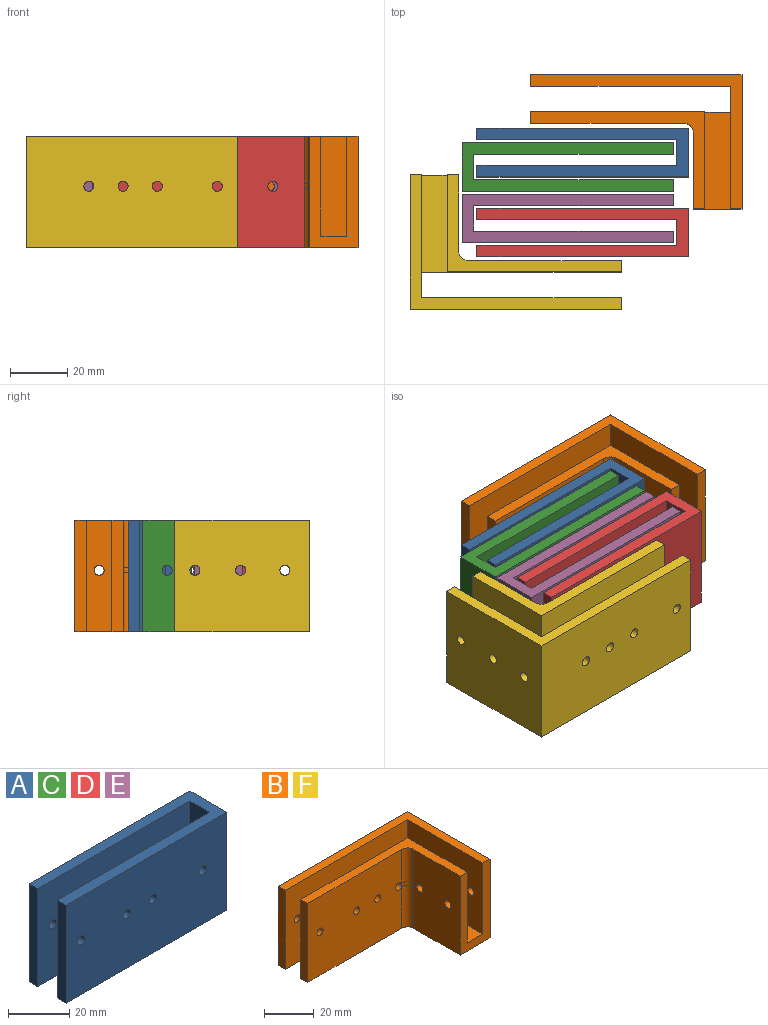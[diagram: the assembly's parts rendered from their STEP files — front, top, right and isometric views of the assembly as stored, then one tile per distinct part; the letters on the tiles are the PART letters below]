
ASSEMBLY  parts=6 mates=8
PART A: 19 faces, bbox 74x17x39 mm
  f0: plane 39x9mm, normal (-1,0,0), area 341.4mm2, adj f1,f7,f8,f9,f18
  f1: plane 70x39mm, normal (0,1,0), area 2691.5mm2, adj f0,f2,f8,f9,f14,f15,f16,f17
  f2: plane 39x4mm, normal (-1,0,0), area 156mm2, adj f1,f3,f8,f9
  f3: plane 74x39mm, normal (0,-1,0), area 2847.5mm2, adj f2,f4,f8,f9,f14,f15,f16,f17
  f4: plane 39x17mm, normal (1,0,0), area 653.4mm2, adj f3,f5,f8,f9,f18
  f5: plane 74x39mm, normal (0,1,0), area 2847.5mm2, adj f4,f6,f8,f9,f10,f11,f12,f13
  f6: plane 39x4mm, normal (-1,0,0), area 156mm2, adj f5,f7,f8,f9
  f7: plane 70x39mm, normal (0,-1,0), area 2691.5mm2, adj f0,f6,f8,f9,f10,f11,f12,f13
  f8: plane 74x17mm, normal (0,0,-1), area 628mm2, adj f0,f1,f2,f3,f4,f5,f6,f7
  f9: plane 74x17mm, normal (0,0,1), area 628mm2, adj f0,f1,f2,f3,f4,f5,f6,f7
  f10: cylinder r=1.75mm len=4mm, axis (0,-1,0), area 44mm2, adj f5,f7
  f11: cylinder r=1.75mm len=4mm, axis (0,-1,0), area 44mm2, adj f5,f7
  f12: cylinder r=1.75mm len=4mm, axis (0,-1,0), area 44mm2, adj f5,f7
  f13: cylinder r=1.75mm len=4mm, axis (0,-1,0), area 44mm2, adj f5,f7
  f14: cylinder r=1.75mm len=4mm, axis (0,-1,0), area 44mm2, adj f1,f3
  f15: cylinder r=1.75mm len=4mm, axis (0,-1,0), area 44mm2, adj f1,f3
  f16: cylinder r=1.75mm len=4mm, axis (0,-1,0), area 44mm2, adj f1,f3
  f17: cylinder r=1.75mm len=4mm, axis (0,-1,0), area 44mm2, adj f1,f3
  f18: cylinder r=1.75mm len=4mm, axis (-1,0,0), area 44mm2, adj f0,f4
PART B: 31 faces, bbox 74x47x39 mm
  f0: plane 34x9mm, normal (0,0,1), area 306mm2, adj f2,f3,f8,f12
  f1: plane 39x4mm, normal (-1,0,0), area 156mm2, adj f2,f10,f11,f13
  f2: plane 70x39mm, normal (0,1,0), area 2376.5mm2, adj f0,f1,f3,f11,f12,f13,f15,f16
  f3: plane 43x39mm, normal (-1,0,0), area 1512.1mm2, adj f0,f2,f4,f8,f11,f14,f25,f26
  f4: plane 70x39mm, normal (0,-1,0), area 2691.5mm2, adj f3,f5,f11,f14,f19,f20,f21,f22
  f5: plane 39x4mm, normal (-1,0,0), area 156mm2, adj f4,f6,f11,f14
  f6: plane 74x39mm, normal (0,1,0), area 2847.5mm2, adj f5,f7,f11,f14,f19,f20,f21,f22
  f7: plane 47x39mm, normal (1,0,0), area 1804.1mm2, adj f6,f8,f11,f14,f25,f26,f27
  f8: plane 39x17mm, normal (0,-1,0), area 348mm2, adj f0,f3,f7,f9,f11,f12,f13,f14
  f9: plane 39x26.51mm, normal (-1,0,0), area 1014.3mm2, adj f8,f11,f13,f23,f24,f28,f29,f30
  f10: plane 53.5x39mm, normal (0,-1,0), area 2048.3mm2, adj f1,f11,f13,f15,f16,f17,f18,f28
  f11: plane 74x47mm, normal (0,0,-1), area 1140.6mm2, adj f1,f2,f3,f4,f5,f6,f7,f8
  f12: plane 35x34mm, normal (1,0,0), area 1170.8mm2, adj f0,f2,f8,f13,f23,f24
  f13: plane 61x34mm, normal (0,0,1), area 366.6mm2, adj f1,f2,f8,f9,f10,f12,f30
  f14: plane 74x47mm, normal (0,0,1), area 468mm2, adj f3,f4,f5,f6,f7,f8
  f15: cylinder r=1.75mm len=4mm, axis (0,1,0), area 44mm2, adj f2,f10,f29
  f16: cylinder r=1.75mm len=4mm, axis (0,1,0), area 44mm2, adj f2,f10
  f17: cylinder r=1.75mm len=4mm, axis (0,1,0), area 44mm2, adj f2,f10
  f18: cylinder r=1.75mm len=4mm, axis (0,1,0), area 44mm2, adj f2,f10
  f19: cylinder r=1.75mm len=4mm, axis (0,1,0), area 44mm2, adj f4,f6
  f20: cylinder r=1.75mm len=4mm, axis (0,1,0), area 44mm2, adj f4,f6
  f21: cylinder r=1.75mm len=4mm, axis (0,1,0), area 44mm2, adj f4,f6
  f22: cylinder r=1.75mm len=4mm, axis (0,1,0), area 44mm2, adj f4,f6
  f23: cylinder r=1.75mm len=4mm, axis (-1,0,0), area 44mm2, adj f9,f12
  f24: cylinder r=1.75mm len=4mm, axis (-1,0,0), area 44mm2, adj f9,f12
  f25: cylinder r=1.75mm len=4mm, axis (-1,0,0), area 44mm2, adj f3,f7
  f26: cylinder r=1.75mm len=4mm, axis (-1,0,0), area 44mm2, adj f3,f7
  f27: cylinder r=1.75mm len=4mm, axis (-1,0,0), area 44mm2, adj f3,f7
  f28: cylinder r=3.5mm len=20.6mm, axis (0,0,1), area 113.2mm2, adj f9,f10,f11,f29
  f29: bspline ~3.5x3.5mm, area 9.6mm2, adj f9,f15,f28,f30
  f30: cylinder r=3.5mm len=16.6mm, axis (0,0,1), area 91.3mm2, adj f9,f10,f13,f29
PART C: same geometry as A
PART D: same geometry as A
PART E: same geometry as A
PART F: same geometry as B
PLACE A t=(-3.3,13.58,0)mm
PLACE B t=(15.52,82.34,0)mm
PLACE C rot(axis=(0,0,1),180deg) t=(-65.5,8.5,0)mm
PLACE D t=(-3.3,-14.39,0)mm
PLACE E rot(axis=(0,0,-1),180deg) t=(-65.5,-9.43,0)mm
PLACE F rot(axis=(0,0,-1),180deg) t=(-83.75,-82.71,0)mm
MATE planar A.f9 <-> D.f9  axis (0,0,1) through (-33.8,18.08,39)mm
MATE planar A.f9 <-> E.f9  axis (0,0,1) through (-29.79,13.58,39)mm
MATE planar C.f18 <-> E.f18  axis (-1,0,0) through (-74,8.5,21.5)mm
MATE planar E.f9 <-> A.f9  axis (0,0,1) through (-37,-0.93,39)mm
MATE planar F.f11 <-> B.f11  axis (0,0,-1) through (-92.25,-17.71,0)mm
MATE planar E.f8 <-> F.f11  axis (0,0,-1) through (-74,-9.43,0)mm
MATE planar D.f9 <-> C.f9  axis (0,0,1) through (-29.79,-14.39,39)mm
MATE planar D.f4 <-> A.f18  axis (1,0,0) through (5.2,-14.39,19.47)mm
